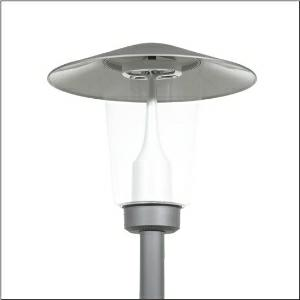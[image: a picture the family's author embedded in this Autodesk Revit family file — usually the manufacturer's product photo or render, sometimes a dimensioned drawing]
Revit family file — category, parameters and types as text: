
# Revit family: pilzleuchte___st1_2a_5xa5235ef14h_3712
name_source: partatom
category: Lighting Fixtures
units: mm (PartAtom-declared; Revit-internal decimal feet)

## family parameters
Cut with Voids When Loaded = No
Host = Face
Light Source = No
Part Type = Normal
Room Calculation Point = No
Round Connector Dimension = Use Diameter
Shared = No

## types (1)
- --- (1 x LED, 1550 lm, 10.5 W, 3000K)
    Apparent Load = 11 VA
    CIE Flux Codes = 24 61 93 98 100
    Color Rendering = 70
    Color Temperature = 3000K
    Default Elevation = 1800 mm
    Description = Mushroom Luminaire, mast luminaire, Module 540 iQ-SR, primary light control with 3 zone facetted reflector, of plastic, silver coated, highly specular, structured, primary optical cover: cover, of PMMA, transparent, light distribution: ST1.2a, light emission: direct distribution, primary light characteristic: asymmetric, installation type: post-top, LED, High Power LED, rated luminous flux: 1.550lm, luminous efficacy: 148lm/W, light colour: 730, colour temperature: 3000K, control gear: ECG iQ, control: Auto-Match, Temp-Guard, Lumen-Switch, Night-Set, Smart-Wire, Light-Fading, Desk-Remote (wireless, voltage-free reading and setting of iQ features in the workshop via application-optimized NFC function/RFID function), optimised constant luminous flux control (CLO 2.0), Street-Remote, presetting dimming logarithmic, with terminal, 6-pole, max. 2.5mm², mains connection: 220..240V, AC, 50/60Hz, start of lifetime: 11W, end of lifetime: 11W, reduction: 5W, luminaire housing, upper part, of glass-fibre reinforced polyester, coated, Siteco® metallic grey (DB 702S), diameter: 650mm, height: 586mm, spigot size: d x l = 76 x 70mm (post-top) | with reducer (optional accessory) 60 x 70mm, post-top mast mounting element, of diecast aluminium, coated, Siteco® metallic grey (DB 702S), Module 540 iQ-SR, traffic white (RAL 9016), equipment: standard, protection rating (complete): IP65, insulation class (complete): insulation class II (safety insulation), certification: CE, ENEC, VDE, packaging unit: 1 piece

Light Distribution: ST1.2a
    Height = 586 mm
    Lamp = 1 x LED
    Lamp Light Flux = 1550 lm
    Lamp Power = 10.5 W
    Lamp count = 1
    Length = 650 mm
    Luminous efficacy = 148 lm/W
    Manufacturer = Siteco
    ModVariant = No
    Model = 5XA5235EF14H
    Number of Poles = 1
    OnlyDefault = Yes
    Power Factor = 1
    Product Name = Pilzleuchte | ST1.2a
    Product group = mast luminaire | pylon top
    ProductGroupID = 6100
    Protection Class = Protection class II
    Protection Degree = IP 65
    RLX_Detail_Level = 1
    RlxData = <blob elided: 123021 chars, md5=055e8e8d>
    Socket = socket
    Standby Power = 0 W
    System Light Flux = 1550 lm
    System Power = 11 W
    Type Comments = factory setting: luminous flux: 100 % | dim-lin: 254 | 419 mA
    Type Image = l_1006077.jpg
    URL = http://relux.com
    VarID = @adj_072011
    Voltage = 0 V
    Weight = 0.00 kg
    Width = 0 mm  [stored 0 ft]

note: [stored X ft] marks values corroborated as IEEE doubles in the binary element streams (Revit-internal decimal feet)

## geometry (parser evidence)
native form markers: Blend x4, Sweep x12
no freeform markers — native parametric forms only
